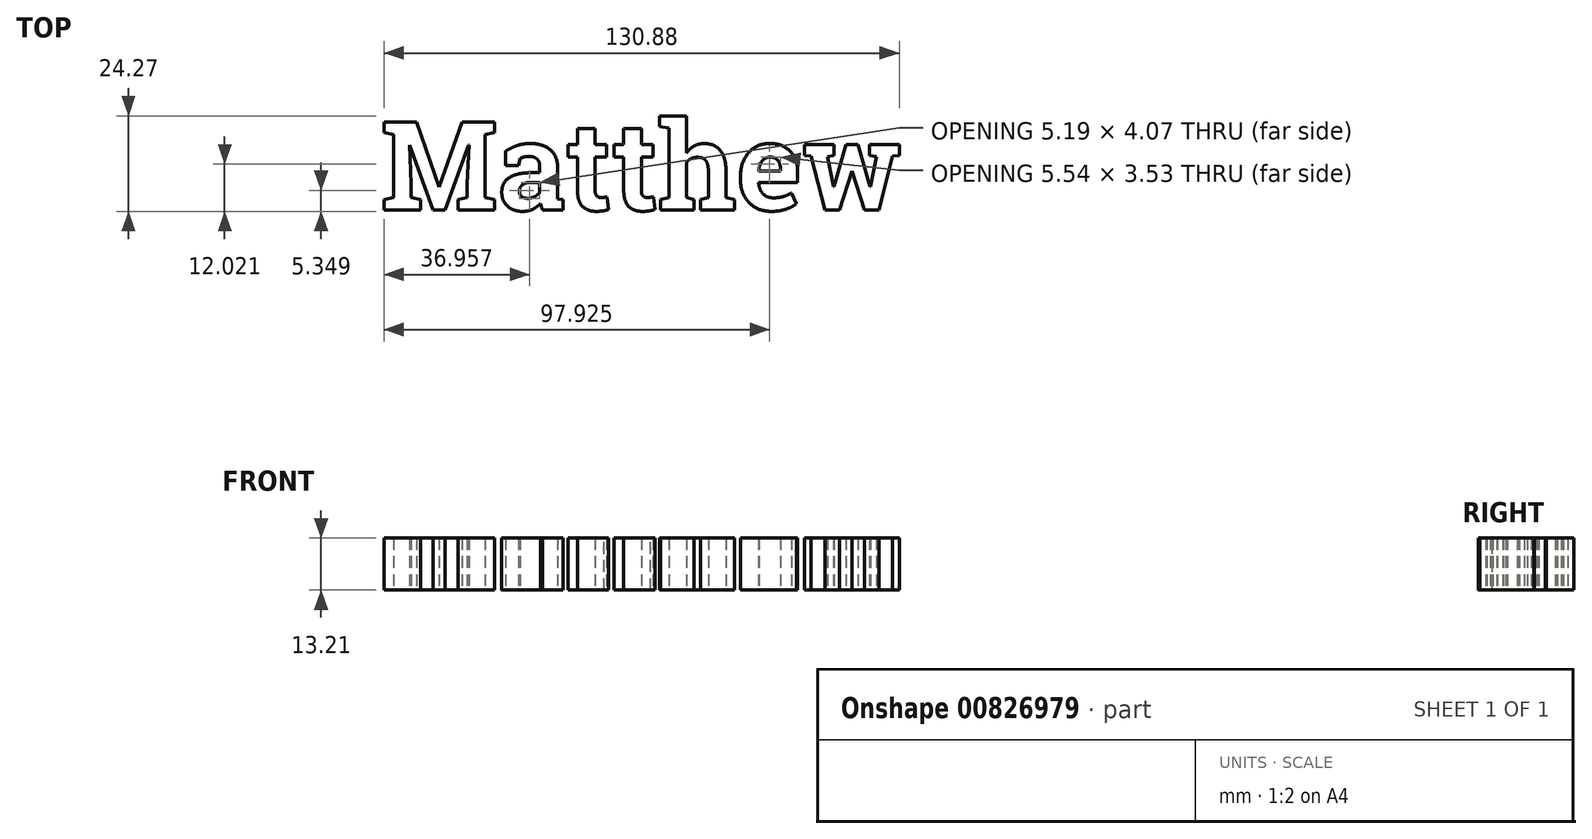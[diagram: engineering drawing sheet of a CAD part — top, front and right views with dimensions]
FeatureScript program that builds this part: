
annotation { "Feature Type Name" : "Feature", "Feature Type Description" : "" }
export const myFeature = defineFeature(function(context is Context, id is Id, definition is map)
    precondition{}
    {
        {
            var Q0;
            Q0=qCreatedBy(makeId("Top.planeOp"),FACE);
            var sketch = newSketch(context, id + "F0", { "sketchPlane" : qUnion([Q0])});
            skText(sketch, "E0", { "text": "Matthew", "fontName": "RobotoSlab-Bold.ttf"});
            const initialGuessF0  = {"E0": [-0.0568, 0.00152, 1, 0, 0.02264]};
            skSetInitialGuess(sketch, initialGuessF0);
            skSolve(sketch);
        }
        {
            var Q0;
            Q0 = qSketchRegion(id + "F0", true);
            extrude(context, id + "F1", {"entities" : qUnion([Q0]), "depth" : 13.2 * mm, "offsetDistance" : 25.4 * mm});
        }
    });
